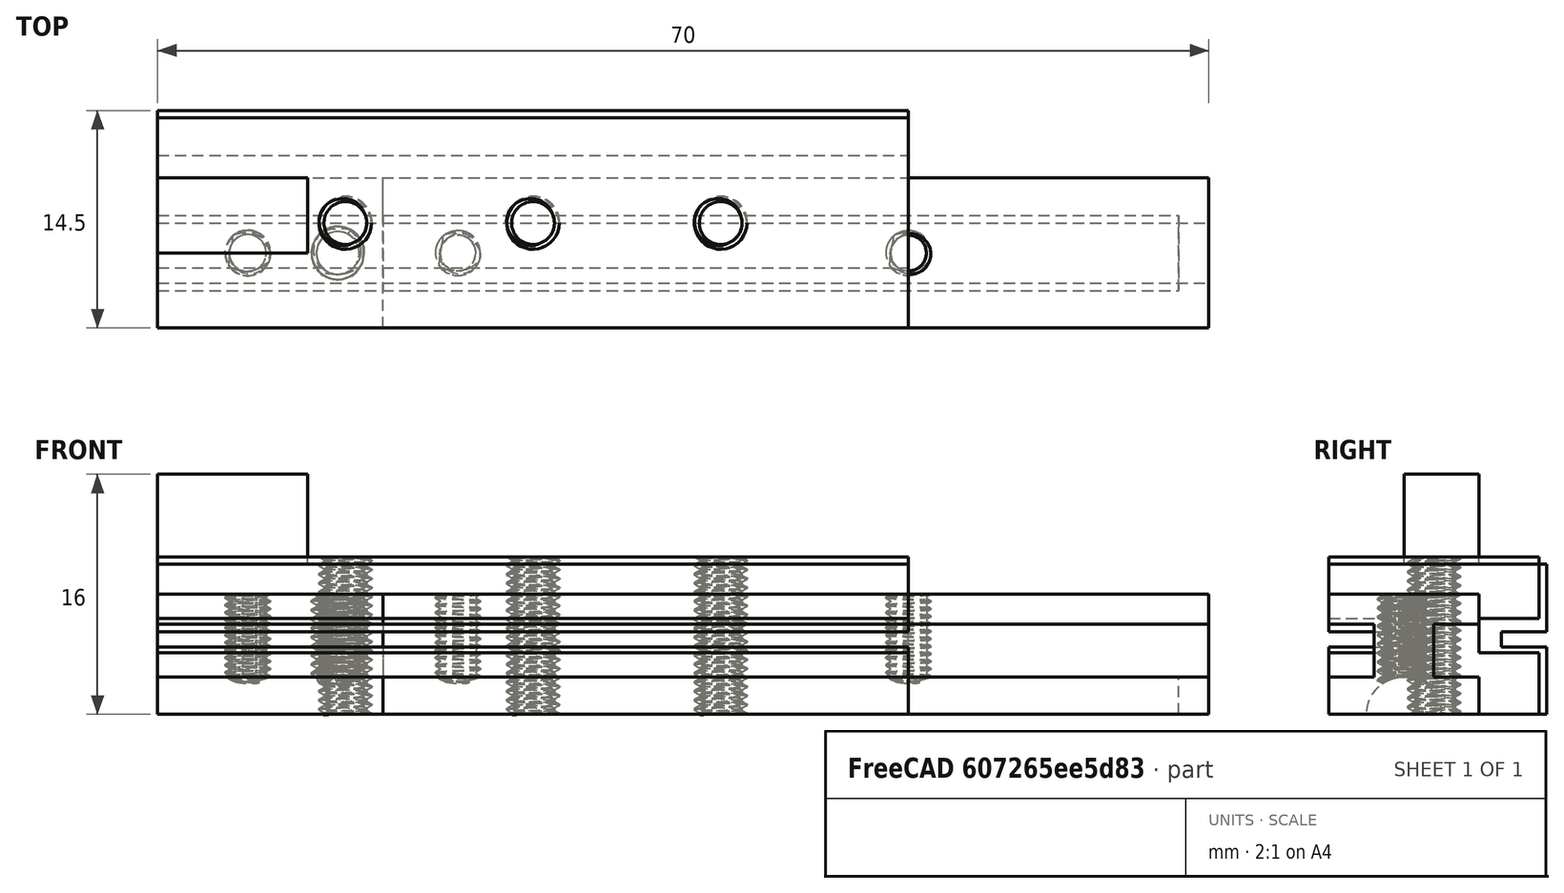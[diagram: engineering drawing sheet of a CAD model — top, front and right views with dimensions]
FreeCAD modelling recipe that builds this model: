
FCSTD DOCUMENT  (FreeCAD 0.18.4R)
Label: Whiteboard_Mount
License: All rights reserved
LicenseURL: http://en.wikipedia.org/wiki/All_rights_reserved
objects: Part::Cut×20, Part::Box×14, Part::FeaturePython×9, Part::Cylinder×2, Part::Fuse×1
note: 46 computed .brp shape members not serialized (recipe doc carries the construction recipe); baked Part::Feature solids carry a one-line shape summary decoded from their .brp

FEATURE [Part::Box] Box  label="Cube"
  AttacherType = Attacher::AttachEngine3D
  Height = 10
  Length = 50
  Width = 14.5
FEATURE [Part::Box] Box001  label="Cube001"
  AttacherType = Attacher::AttachEngine3D
  Height = 1
  Length = 50
  Placement = pos=(0,0,4.5) rot=(0,0,1;0rad)
  Width = 4
FEATURE [Part::Box] Box002  label="Cube002"
  AttacherType = Attacher::AttachEngine3D
  Height = 1
  Length = 50
  Placement = pos=(0,11.5,4.5) rot=(0,0,1;0rad)
  Width = 3
FEATURE [Part::Box] Box003  label="Cube003"
  AttacherType = Attacher::AttachEngine3D
  Height = 16
  Length = 10
  Placement = pos=(0,5,0) rot=(0,0,1;0rad)
  Width = 5
FEATURE [Part::Cut] Cut
  Base = -> Box
  Tool = -> Box001
FEATURE [Part::Cut] Cut001
  Base = -> Cut
  Tool = -> Box002
FEATURE [Part::Fuse] Fusion  label="Test_Slider001"
  Base = -> Box003
  Tool = -> Cut001
FEATURE [Part::Box] Box004  label="Cube004"
  AttacherType = Attacher::AttachEngine3D
  Height = 8
  Length = 70
  Width = 10
FEATURE [Part::Box] Box005  label="Cube005"
  AttacherType = Attacher::AttachEngine3D
  Height = 3.5
  Length = 70
  Placement = pos=(0,0,2.5) rot=(0,0,1;0rad)
  Width = 3
FEATURE [Part::Box] Box006  label="Cube006"
  AttacherType = Attacher::AttachEngine3D
  Height = 3.5
  Length = 70
  Placement = pos=(0,7,2.5) rot=(0,0,1;0rad)
  Width = 3
FEATURE [Part::Cut] Cut002
  Base = -> Box004
  Tool = -> Box005
FEATURE [Part::Cut] Cut003  label="Test_Slider002"
  Base = -> Cut002
  Tool = -> Box006
FEATURE [Part::Cylinder] Cylinder
  Angle = 360
  AttacherType = Attacher::AttachEngine3D
  Height = 68
  Placement = pos=(0,5,0) rot=(0,1,0;1.5708rad)
  Radius = 2.5
FEATURE [Part::Cut] Cut004
  Base = -> Cut003
  Tool = -> Cylinder
FEATURE [Part::FeaturePython] Screw  label="M3x30-Screw"  # Fasteners workbench fastener (typed FeaturePython)
  Placement = pos=(20,5,28) rot=(0,0,1;0rad)
  diameter = 4
  invert = false
  length = 2
  matchOuter = false
  offset = 0
  thread = true
  type = 13
FEATURE [Part::FeaturePython] Screw001  label="M3x30-Screw001"  # Fasteners workbench fastener (typed FeaturePython)
  Placement = pos=(50,5,27) rot=(0,0,1;0rad)
  diameter = 4
  invert = false
  length = 2
  matchOuter = false
  offset = 0
  thread = true
  type = 13
FEATURE [Part::Cut] Cut005
  Base = -> Cut004
  Tool = -> Screw
FEATURE [Part::Cut] Cut006
  Base = -> Cut005
  Tool = -> Screw001
FEATURE [Part::FeaturePython] ScrewTap  label="M3x27.0-ScrewTap"  # Fasteners workbench fastener (typed FeaturePython)
  Placement = pos=(6,5,10) rot=(0,0,1;0rad)
  diameter = 4
  invert = false
  length = 27
  matchOuter = false
  offset = 0
  thread = true
FEATURE [Part::Box] Box012  label="Cube012"
  AttacherType = Attacher::AttachEngine3D
  Height = 8
  Length = 70
  Width = 10
FEATURE [Part::Box] Box013  label="Cube013"
  AttacherType = Attacher::AttachEngine3D
  Height = 3.5
  Length = 70
  Placement = pos=(0,0,2.5) rot=(0,0,1;0rad)
  Width = 3
FEATURE [Part::Box] Box014  label="Cube014"
  AttacherType = Attacher::AttachEngine3D
  Height = 3.5
  Length = 70
  Placement = pos=(0,7,2.5) rot=(0,0,1;0rad)
  Width = 3
FEATURE [Part::Cut] Cut014
  Base = -> Box012
  Tool = -> Box013
FEATURE [Part::Cut] Cut015  label="Test_Slider003"
  Base = -> Cut014
  Tool = -> Box014
FEATURE [Part::FeaturePython] Screw002  label="M3x30-Screw002"  # Fasteners workbench fastener (typed FeaturePython)
  Placement = pos=(50,5,27) rot=(0,0,1;0rad)
  diameter = 4
  invert = false
  length = 2
  matchOuter = false
  offset = 0
  thread = true
  type = 13
FEATURE [Part::Cylinder] Cylinder006
  Angle = 360
  AttacherType = Attacher::AttachEngine3D
  Height = 68
  Placement = pos=(0,5,0) rot=(0,1,0;1.5708rad)
  Radius = 2.5
FEATURE [Part::Cut] Cut017
  Base = -> Cut015
  Tool = -> Cylinder006
FEATURE [Part::FeaturePython] Screw003  label="M3x30-Screw003"  # Fasteners workbench fastener (typed FeaturePython)
  Placement = pos=(20,5,28) rot=(0,0,1;0rad)
  diameter = 4
  invert = false
  length = 2
  matchOuter = false
  offset = 0
  thread = true
  type = 13
FEATURE [Part::Cut] Cut016
  Base = -> Cut017
  Tool = -> Screw003
FEATURE [Part::Cut] Cut018
  Base = -> Cut016
  Tool = -> Screw002
FEATURE [Part::Box] Box015  label="Cube015"
  AttacherType = Attacher::AttachEngine3D
  Height = 10
  Length = 70
  Placement = pos=(15,0,0) rot=(0,0,1;0rad)
  Width = 10
FEATURE [Part::Cut] Cut019
  Base = -> Cut018
  Tool = -> Box015
FEATURE [Part::Cut] Cut020
  Base = -> Cut019
  Tool = -> ScrewTap
FEATURE [Part::FeaturePython] ScrewTap001  label="(M3.5)x27.0-ScrewTap"  # Fasteners workbench fastener (typed FeaturePython)
  Placement = pos=(12,5,9) rot=(0,0,1;0rad)
  diameter = 5
  invert = false
  length = 27
  matchOuter = false
  offset = 0
  thread = true
FEATURE [Part::Cut] Cut021
  Base = -> Cut020
  Tool = -> ScrewTap001
FEATURE [Part::Box] Box016  label="Cube016"
  AttacherType = Attacher::AttachEngine3D
  Height = 10.5
  Length = 50
  Width = 14
FEATURE [Part::Box] Box017  label="Cube017"
  AttacherType = Attacher::AttachEngine3D
  Height = 2.3
  Length = 50
  Placement = pos=(0,0,4.1) rot=(0,0,1;0rad)
  Width = 4
FEATURE [Part::Box] Box018  label="Cube018"
  AttacherType = Attacher::AttachEngine3D
  Height = 2.3
  Length = 50
  Placement = pos=(0,10,4.1) rot=(0,0,1;0rad)
  Width = 4
FEATURE [Part::Cut] Cut022
  Base = -> Box016
  Tool = -> Box017
FEATURE [Part::Cut] Cut023
  Base = -> Cut022
  Tool = -> Box018
FEATURE [Part::FeaturePython] ScrewTap002  label="(M3.5)x20.0-ScrewTap"  # Fasteners workbench fastener (typed FeaturePython)
  Placement = pos=(25,7,15) rot=(0,0,1;0rad)
  diameter = 5
  invert = false
  length = 20
  matchOuter = false
  offset = 0
  thread = true
FEATURE [Part::FeaturePython] ScrewTap003  label="(M3.5)x20.0-ScrewTap003"  # Fasteners workbench fastener (typed FeaturePython)
  Placement = pos=(12.5,7,15) rot=(0,0,1;0rad)
  diameter = 5
  invert = false
  length = 20
  matchOuter = false
  offset = 0
  thread = true
FEATURE [Part::FeaturePython] ScrewTap004  label="(M3.5)x20.0-ScrewTap002"  # Fasteners workbench fastener (typed FeaturePython)
  Placement = pos=(37.5,7,15) rot=(0,0,1;0rad)
  diameter = 5
  invert = false
  length = 20
  matchOuter = false
  offset = 0
  thread = true
FEATURE [Part::Cut] Cut024
  Base = -> Cut023
  Tool = -> ScrewTap002
FEATURE [Part::Cut] Cut025
  Base = -> Cut024
  Tool = -> ScrewTap004
FEATURE [Part::Cut] Cut026  label="SliderV4"
  Base = -> Cut025
  Tool = -> ScrewTap003
